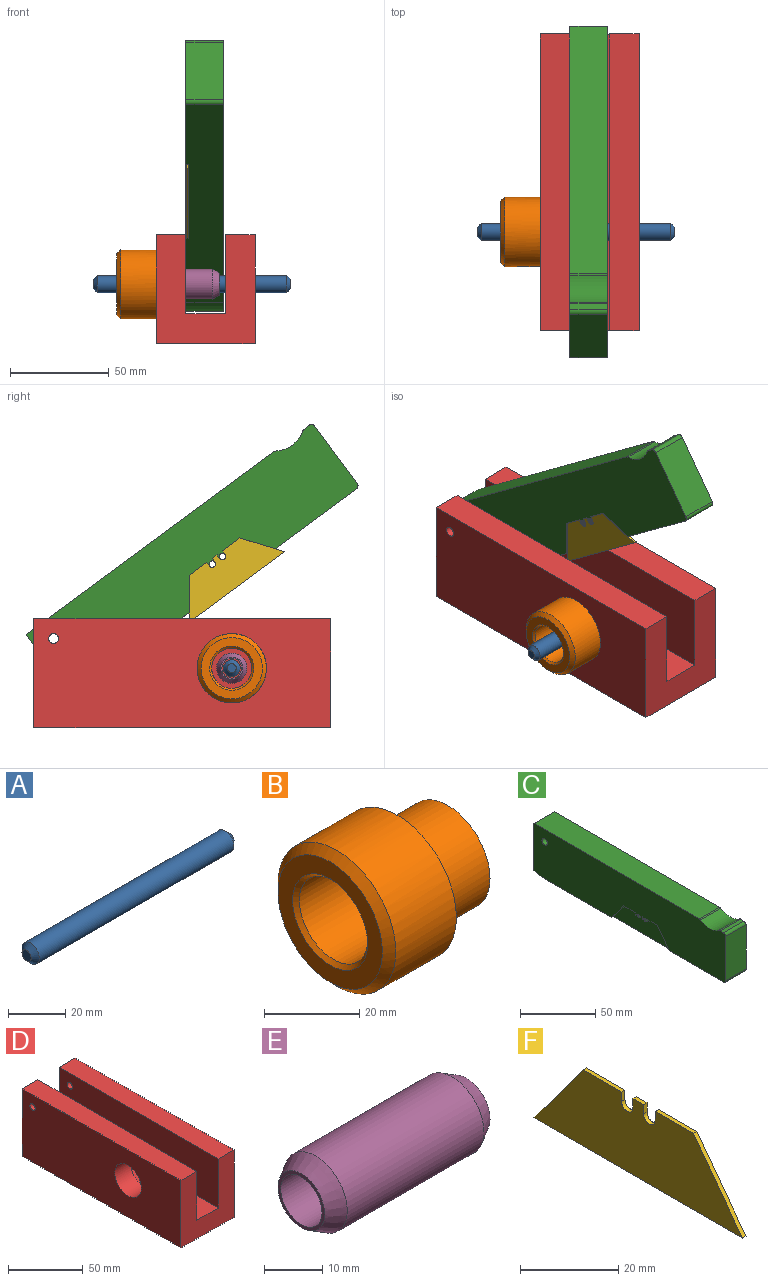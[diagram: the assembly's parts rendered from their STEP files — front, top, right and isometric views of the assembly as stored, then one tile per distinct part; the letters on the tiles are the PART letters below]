
ASSEMBLY  parts=6 mates=5
PART A: 5 faces, bbox 100x8.5x8.5 mm
  f0: cylinder r=4.25mm len=96mm, axis (1,0,0), area 2563.5mm2, adj f3,f4
  f1: plane 4.5x4.5mm, normal (-1,0,0), area 15.9mm2, adj f4
  f2: plane 4.5x4.5mm, normal (1,0,0), area 15.9mm2, adj f3
  f3: cone r=4.25mm half-angle=45deg, axis (-1,0,0), area 57.8mm2, adj f0,f2
  f4: cone r=2.25mm half-angle=45deg, axis (1,0,0), area 57.8mm2, adj f0,f1
PART B: 8 faces, bbox 35x35x35 mm
  f0: cylinder r=17.5mm len=35mm, axis (1,0,0), area 1979.2mm2, adj f4,f6
  f1: plane 25x25mm, normal (1,0,0), area 167.2mm2, adj f2,f5
  f2: cylinder r=10.15mm len=34mm, axis (1,0,0), area 2168.3mm2, adj f1,f7
  f3: plane 31x31mm, normal (-1,0,0), area 364.2mm2, adj f6,f7
  f4: plane 35x35mm, normal (1,0,0), area 471.2mm2, adj f0,f5
  f5: cylinder r=12.5mm len=25mm, axis (-1,0,0), area 1178.1mm2, adj f1,f4
  f6: cone r=15.5mm half-angle=45deg, axis (1,0,0), area 293.2mm2, adj f0,f3
  f7: cone r=10.15mm half-angle=45deg, axis (-1,0,0), area 94.6mm2, adj f2,f3
PART C: 26 faces, bbox 19x180x40 mm
  f0: plane 180x40mm, normal (1,0,0), area 7119mm2, adj f1,f11,f12,f14,f15,f16,f17,f19
  f1: plane 155.36x19mm, normal (0,0,1), area 2951.8mm2, adj f0,f11,f13,f20
  f2: plane 15x11.15mm, normal (0,0.8,-0.6), area 28mm2, adj f8,f12,f13,f18
  f3: plane 15x11.15mm, normal (0,-0.8,-0.6), area 28mm2, adj f9,f12,f13,f18
  f4: plane 2.35x1.5mm, normal (0,-1,0), area 3.5mm2, adj f5,f13,f18,f25
  f5: plane 3.05x1.5mm, normal (0,0,-1), area 4.6mm2, adj f4,f6,f13,f18
  f6: plane 2.35x1.5mm, normal (0,1,0), area 3.5mm2, adj f5,f13,f18,f24
  f7: plane 2.35x1.5mm, normal (0,-1,0), area 3.5mm2, adj f8,f13,f18,f24
  f8: plane 11.05x1.5mm, normal (0,0,-1), area 16.6mm2, adj f2,f7,f13,f18
  f9: plane 11.05x1.5mm, normal (0,0,-1), area 16.6mm2, adj f3,f10,f13,f18
  f10: plane 2.35x1.5mm, normal (0,1,0), area 3.5mm2, adj f9,f13,f18,f25
  f11: plane 38.28x19mm, normal (0,1,0), area 727.4mm2, adj f0,f1,f13,f17
  f12: plane 168x19mm, normal (0,0,-1), area 3110.9mm2, adj f0,f2,f3,f13,f17,f18,f23
  f13: plane 180x40mm, normal (-1,0,0), area 6499.6mm2, adj f1,f2,f3,f4,f5,f6,f7,f8
  f14: plane 19x3.36mm, normal (0,0,1), area 63.8mm2, adj f0,f13,f21,f22
  f15: plane 36x19mm, normal (0,-1,0), area 684mm2, adj f0,f13,f22,f23
  f16: cylinder r=2.5mm len=19mm, axis (-1,0,0), area 298.5mm2, adj f0,f13
  f17: cylinder r=30mm len=19mm, axis (-1,0,0), area 193.7mm2, adj f0,f11,f12,f13
  f18: plane 54.05x15mm, normal (-1,0,0), area 619.5mm2, adj f2,f3,f4,f5,f6,f7,f8,f9
  f19: cylinder r=15mm len=19mm, axis (1,0,0), area 343.8mm2, adj f0,f13,f20,f21
  f20: cylinder r=2mm len=19mm, axis (1,0,0), area 22.9mm2, adj f0,f1,f13,f19
  f21: cylinder r=2mm len=19mm, axis (1,0,0), area 22.9mm2, adj f0,f13,f14,f19
  f22: cylinder r=2mm len=19mm, axis (-1,0,0), area 59.7mm2, adj f0,f13,f14,f15
  f23: cylinder r=2mm len=19mm, axis (1,0,0), area 59.7mm2, adj f0,f12,f13,f15
  f24: cylinder r=1.65mm len=19mm, axis (-1,0,0), area 189.2mm2, adj f0,f6,f7,f13,f18
  f25: cylinder r=1.65mm len=19mm, axis (-1,0,0), area 189.2mm2, adj f0,f4,f10,f13,f18
PART D: 14 faces, bbox 50x150x55 mm
  f0: plane 150x20mm, normal (0,0,1), area 3000mm2, adj f1,f7,f8,f9
  f1: plane 150x40mm, normal (1,0,0), area 5489.5mm2, adj f0,f2,f8,f9,f10,f13
  f2: plane 150x15mm, normal (0,0,1), area 2250mm2, adj f1,f3,f8,f9
  f3: plane 150x55mm, normal (-1,0,0), area 7739.5mm2, adj f2,f4,f8,f9,f10,f13
  f4: plane 150x50mm, normal (0,0,-1), area 7500mm2, adj f3,f5,f8,f9
  f5: plane 150x55mm, normal (1,0,0), area 8173.6mm2, adj f4,f6,f8,f9,f11,f12
  f6: plane 150x15mm, normal (0,0,1), area 2250mm2, adj f5,f7,f8,f9
  f7: plane 150x40mm, normal (-1,0,0), area 5923.6mm2, adj f0,f6,f8,f9,f11,f12
  f8: plane 55x50mm, normal (0,1,0), area 1950mm2, adj f0,f1,f2,f3,f4,f5,f6,f7
  f9: plane 55x50mm, normal (0,-1,0), area 1950mm2, adj f0,f1,f2,f3,f4,f5,f6,f7
  f10: cylinder r=12.5mm len=25mm, axis (-1,0,0), area 1178.1mm2, adj f1,f3
  f11: cylinder r=4.25mm len=15mm, axis (-1,0,0), area 400.6mm2, adj f5,f7
  f12: cylinder r=2.5mm len=15mm, axis (-1,0,0), area 235.6mm2, adj f5,f7
  f13: cylinder r=2.5mm len=15mm, axis (-1,0,0), area 235.6mm2, adj f1,f3
PART E: 6 faces, bbox 40x15.3x15.3 mm
  f0: cylinder r=5mm len=40mm, axis (1,0,0), area 1256.6mm2, adj f2,f3
  f1: cylinder r=7.65mm len=33.07mm, axis (1,0,0), area 1589.6mm2, adj f4,f5
  f2: plane 11.3x11.3mm, normal (-1,0,0), area 21.7mm2, adj f0,f5
  f3: plane 11.3x11.3mm, normal (1,0,0), area 21.7mm2, adj f0,f4
  f4: cone r=7.65mm half-angle=30deg, axis (-1,0,0), area 167.1mm2, adj f1,f3
  f5: cone r=5.65mm half-angle=30deg, axis (1,0,0), area 167.1mm2, adj f1,f2
PART F: 14 faces, bbox 1x60x19 mm
  f0: cylinder r=1.65mm len=3.3mm, axis (-1,0,0), area 5.2mm2, adj f1,f11,f12,f13
  f1: plane 2.35x1mm, normal (0,1,0), area 2.3mm2, adj f0,f2,f12,f13
  f2: plane 3.05x1mm, normal (0,0,1), area 3.1mm2, adj f1,f3,f12,f13
  f3: plane 2.35x1mm, normal (0,-1,0), area 2.4mm2, adj f2,f4,f12,f13
  f4: cylinder r=1.65mm len=3.3mm, axis (-1,0,0), area 5.2mm2, adj f3,f5,f12,f13
  f5: plane 2.35x1mm, normal (0,1,0), area 2.3mm2, adj f4,f6,f12,f13
  f6: plane 11.05x1mm, normal (0,0,1), area 11mm2, adj f5,f7,f12,f13
  f7: plane 19x14.13mm, normal (0,-0.8,0.6), area 23.7mm2, adj f6,f8,f12,f13
  f8: plane 60x1mm, normal (0,0,-1), area 60mm2, adj f7,f9,f12,f13
  f9: plane 19x14.13mm, normal (0,0.8,0.6), area 23.7mm2, adj f8,f10,f12,f13
  f10: plane 11.05x1mm, normal (0,0,1), area 11.1mm2, adj f9,f11,f12,f13
  f11: plane 2.35x1mm, normal (0,-1,0), area 2.3mm2, adj f0,f10,f12,f13
  f12: plane 60x19mm, normal (1,0,0), area 847.6mm2, adj f0,f1,f2,f3,f4,f5,f6,f7
  f13: plane 60x19mm, normal (-1,0,0), area 847.6mm2, adj f0,f1,f2,f3,f4,f5,f6,f7
PLACE A t=(13.27,-30.85,21.25)mm
PLACE B t=(20.17,-30.85,21.25)mm
PLACE C rot(axis=(-1,0,0),36.4deg) t=(19.67,-30.22,113.19)mm
PLACE D t=(20.17,-30.85,21.25)mm fixed
PLACE E t=(17.08,-30.85,21.25)mm
PLACE F rot(axis=(-1,0,0),36.4deg) t=(10.42,-30.22,113.19)mm
MATE revolute D.f12 <-> C.f16  axis (1,0,0) through (10.17,109.15,66.25)mm
MATE slider D.f10 <-> A.f3  axis (-1,0,0) through (37.67,19.15,51.25)mm
MATE fastened D.f10 <-> B.f0  axis (-1,0,0) through (-4.83,19.15,51.25)mm
MATE fastened C.f5 <-> F.f2  axis (0,-0.59,-0.8) through (10.92,27.83,107.63)mm
MATE slider E.f0 <-> A.f3  axis (1,0,0) through (-12.92,19.15,51.25)mm
